# Revit family: IS_TonicII_K2916_BIM_DE
name_source: partatom
category: Plumbing Fixtures
revit_build: Autodesk Revit MEP 2016 (Build: 20161004_0715(x64)
units: mm (PartAtom-declared; Revit-internal decimal feet)

## family parameters
Always vertical = No
Cut with Voids When Loaded = No
OmniClass Number = 23.45.05.14.21.11
OmniClass Title = Bath/Shower Units
Part Type = Normal
Room Calculation Point = No
Round Connector Dimension = Use Diameter
Shared = No
Work Plane-Based = No

## types (1)
- K291601 - TONIC II hexagon bath tub 2000x1000mm
    Accessories = www.idealstandard.de\ersatzteile
    AreaUnits = millimeters
    AssetType = Fixed
    BIMObjectName = ISI_IdealStandard_Baths_TonicII_K291601
    BIMobject category = Bath & Spas
    BOSUseNativeGeometries = 1
    BarCode = -2146826265
    BathType = Domestic
    Brand = Ideal Standard
    Brand url = http://www.idealstandard.co.uk
    CodePerformance = -2146826265
    Color = -2146826265
    ConnectionType = Plumbing
    Cost = 0 $
    CurrencyUnit = €
    CurrentRevision = 1
    Date of publishing = 2017_11_10
    Description = -2146826265
    DrainSize = 0 mm  [stored 0 ft]
    DurationUnit = year
    EAN code = https://4015413066532
    Edition number = 1
    ExpectedLife = -2146826265
    Features = -2146826265
    Finish = -2146826265
    HasGrabHandles = No
    IFC Classification = Sanitary Terminal
    IfcExportAs = Ifc Sanitary Terminal Type
    IfcExportType = BATH
    Installation instructions = http://www.idealstandard.de
    InstallationInstructions = www.idealstandard.de\produkte
    LinearUnits = millimeters
    MainColor = White
    MaintenanceInformation = -2146826265
    Manufacturer name = Ideal Standard
    ManufacturerURL = www.idealstandard.com
    Material = Acrylic
    Material main = Acrylic
    MaterialThickness = 0 mm  [stored 0 ft]
    Model = K291601
    ModelNumber = K291601
    ModelReference = IS Sechseck-Badewanne TONIC II, m. Ablauf, 2000x950x480mm, Weiß
    NBS Reference Code = 35-06-08
    NBS Reference Description = Baths
    Name = Baths_TonicII_K291601_IdealStandard
    NettWeight = -2146826265
    Nominal height = 490
    Nominal width = 1000
    NominalDepth = 950 mm  [stored 3.1168 ft]
    NominalHeight = 468 mm
    NominalLength = 950 mm  [stored 3.1168 ft]
    NominalWidth = 2000 mm
    OmniClass Code = 23-31 15 00
    OmniClass Description = Bathtubs
    Product Guid = 846e8933-17bf-4872-99e0-1cbe5b3fa82e
    Product SKU = K2916
    Product certification = -2146826265
    Product data url = https://bimobject.com
    Product family = TONIC II
    Product group = Bath Tub
    Product name = TONIC II hexagon bath tub 2000x1000mm
    Product url = http://www.idealstandard.de
    ProductInformation = www.idealstandard.de/produkte
    QR code = http://bimobject.com
    Shape = -2146826265
    Size = 468 x 950 x 2000mm
    Space = Internal
    SpareParts = www.idealstandard.de/ersatzteile
    Technical description = http://www.idealstandard.de
    URL = http://www.idealstandard.de
    Uniclass 1.4 Code = L7211
    Uniclass 1.4 Description = Baths
    Uniclass 2.0 Code = PR-35-06-08
    Uniclass 2.0 Description = Baths
    Uniclass 2015 Code = Pr_40_20_06_08
    Uniclass 2015 Name = Baths
    Uniclass2015Code = Pr_40_20_06_08
    Uniclass2015Title = Baths
    Uniclass2015Version = Products v1.1
    Version = 1
    VolumeUnits = Litres
    Weight Net (Kg) = 30.5

note: [stored X ft] marks values corroborated as IEEE doubles in the binary element streams (Revit-internal decimal feet)

## geometry (parser evidence)
native form markers: Blend x2, Sweep x3
no freeform markers — native parametric forms only
